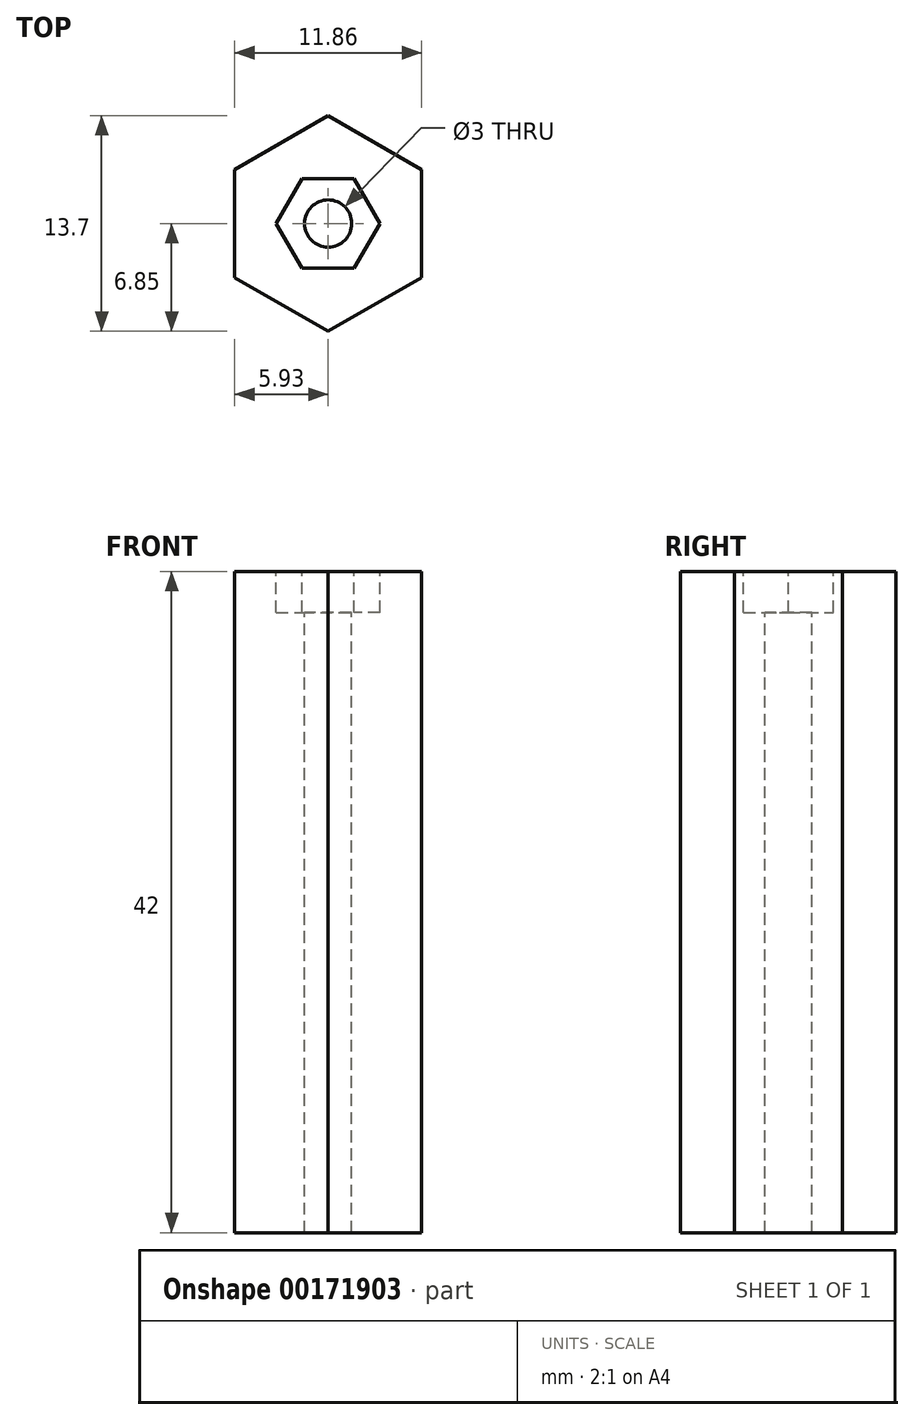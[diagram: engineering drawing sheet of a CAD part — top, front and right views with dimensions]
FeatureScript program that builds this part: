
annotation { "Feature Type Name" : "Feature", "Feature Type Description" : "" }
export const myFeature = defineFeature(function(context is Context, id is Id, definition is map)
    precondition{}
    {
        {
            var Q0;
            Q0=qCreatedBy(makeId("Top.planeOp"),FACE);
            var sketch = newSketch(context, id + "F0", { "sketchPlane" : qUnion([Q0])});
            skCircle(sketch, "E0.cCircle", {"center": v(0, 0) * mm, "radius": 6.85 * mm, "construction": true});
            skLineSegment(sketch, "E0.0", {"start": v(0, -6.85) * mm, "end": v(-5.93, -3.43) * mm});
            skLineSegment(sketch, "E0.1", {"start": v(-5.93, -3.43) * mm, "end": v(-5.93, 3.42) * mm});
            skLineSegment(sketch, "E0.2", {"start": v(-5.93, 3.43) * mm, "end": v(0, 6.85) * mm});
            skLineSegment(sketch, "E0.3", {"start": v(0, 6.85) * mm, "end": v(5.93, 3.43) * mm});
            skLineSegment(sketch, "E0.4", {"start": v(5.93, 3.43) * mm, "end": v(5.93, -3.43) * mm});
            skLineSegment(sketch, "E0.5", {"start": v(5.93, -3.43) * mm, "end": v(0, -6.85) * mm});
            skSolve(sketch);
        }
        {
            var Q0;
            Q0 = qSketchRegion(id + "F0", true);
            extrude(context, id + "F1", {"entities" : qUnion([Q0]), "depth" : 32 * mm});
        }
        {
            var Q0;
            Q0=makeQuery(id+"F1.opExtrude","CAP_FACE",FACE,{"disambiguationData":[OSD([sQuery(id+"F0.wireOp",EDGE,"E0.0"),sQuery(id+"F0.wireOp",EDGE,"E0.1"),sQuery(id+"F0.wireOp",EDGE,"E0.2"),sQuery(id+"F0.wireOp",EDGE,"E0.3"),sQuery(id+"F0.wireOp",EDGE,"E0.4"),sQuery(id+"F0.wireOp",EDGE,"E0.5")])],"isStart":false});
            var sketch = newSketch(context, id + "F2", { "sketchPlane" : qUnion([Q0])});
            skCircle(sketch, "E1", {"center": v(0, 0) * mm, "radius": 2 * mm});
            skSolve(sketch);
        }
        {
            var Q0;
            Q0=sQuery(id+"F2.wireOp",VERTEX,"E1.center");
            var Q1;
            Q1=makeQuery(id+"F1.opExtrude","SWEPT_BODY",BODY,{"disambiguationData":[OSD([sQuery(id+"F0.wireOp",EDGE,"E0.0"),sQuery(id+"F0.wireOp",EDGE,"E0.1"),sQuery(id+"F0.wireOp",EDGE,"E0.2"),sQuery(id+"F0.wireOp",EDGE,"E0.3"),sQuery(id+"F0.wireOp",EDGE,"E0.4"),sQuery(id+"F0.wireOp",EDGE,"E0.5")])]});
            hole(context, id + "F3", {"style" : HoleStyle.C_BORE, "endStyle" : HoleEndStyle.BLIND, "holeDiameter" : 3 * mm, "cBoreDiameter" : 3 * mm, "cBoreDepth" : 40 * mm, "holeDepth" : 40 * mm, "isTappedThrough" : true, "tappedDepth" : 12 * mm, "tapClearance" : 3, "locations" : qUnion([Q0]), "scope" : qUnion([Q1])});
        }
        {
            var Q0;
            Q0=makeQuery(id+"F1.opExtrude","CAP_FACE",FACE,{"disambiguationData":[OSD([sQuery(id+"F0.wireOp",EDGE,"E0.0"),sQuery(id+"F0.wireOp",EDGE,"E0.1"),sQuery(id+"F0.wireOp",EDGE,"E0.2"),sQuery(id+"F0.wireOp",EDGE,"E0.3"),sQuery(id+"F0.wireOp",EDGE,"E0.4"),sQuery(id+"F0.wireOp",EDGE,"E0.5")])],"isStart":false});
            extrude(context, id + "F4", {"entities" : qUnion([Q0]), "operationType" : NewBodyOperationType.ADD, "depth" : 10 * mm});
        }
        {
            var Q0;
            Q0=makeQuery(id+"F4.opExtrude","CAP_FACE",FACE,{"disambiguationData":[OSD([sQuery(id+"F0.wireOp",EDGE,"E0.0"),sQuery(id+"F0.wireOp",EDGE,"E0.1"),sQuery(id+"F0.wireOp",EDGE,"E0.2"),sQuery(id+"F0.wireOp",EDGE,"E0.3"),sQuery(id+"F0.wireOp",EDGE,"E0.4"),sQuery(id+"F0.wireOp",EDGE,"E0.5")])],"isStart":false});
            var sketch = newSketch(context, id + "F5", { "sketchPlane" : qUnion([Q0])});
            skCircle(sketch, "E2.cCircle", {"center": v(0, 0) * mm, "radius": 2.85 * mm, "construction": true});
            skLineSegment(sketch, "E2.0", {"start": v(-1.65, 2.85) * mm, "end": v(1.65, 2.85) * mm});
            skLineSegment(sketch, "E2.1", {"start": v(1.65, 2.85) * mm, "end": v(3.3, 0) * mm});
            skLineSegment(sketch, "E2.2", {"start": v(3.3, 0) * mm, "end": v(1.65, -2.85) * mm});
            skLineSegment(sketch, "E2.3", {"start": v(1.65, -2.85) * mm, "end": v(-1.65, -2.85) * mm});
            skLineSegment(sketch, "E2.4", {"start": v(-1.65, -2.85) * mm, "end": v(-3.3, 0) * mm});
            skLineSegment(sketch, "E2.5", {"start": v(-3.3, 0) * mm, "end": v(-1.65, 2.85) * mm});
            skPoint(sketch, "E2.0.midPoint", {"position": v(0, 2.85) * mm});
            skSolve(sketch);
        }
        {
            var Q0;
            Q0 = qSketchRegion(id + "F5", true);
            extrude(context, id + "F6", {"entities" : qUnion([Q0]), "operationType" : NewBodyOperationType.REMOVE, "oppositeDirection" : true, "depth" : 2.6 * mm});
        }
    });
